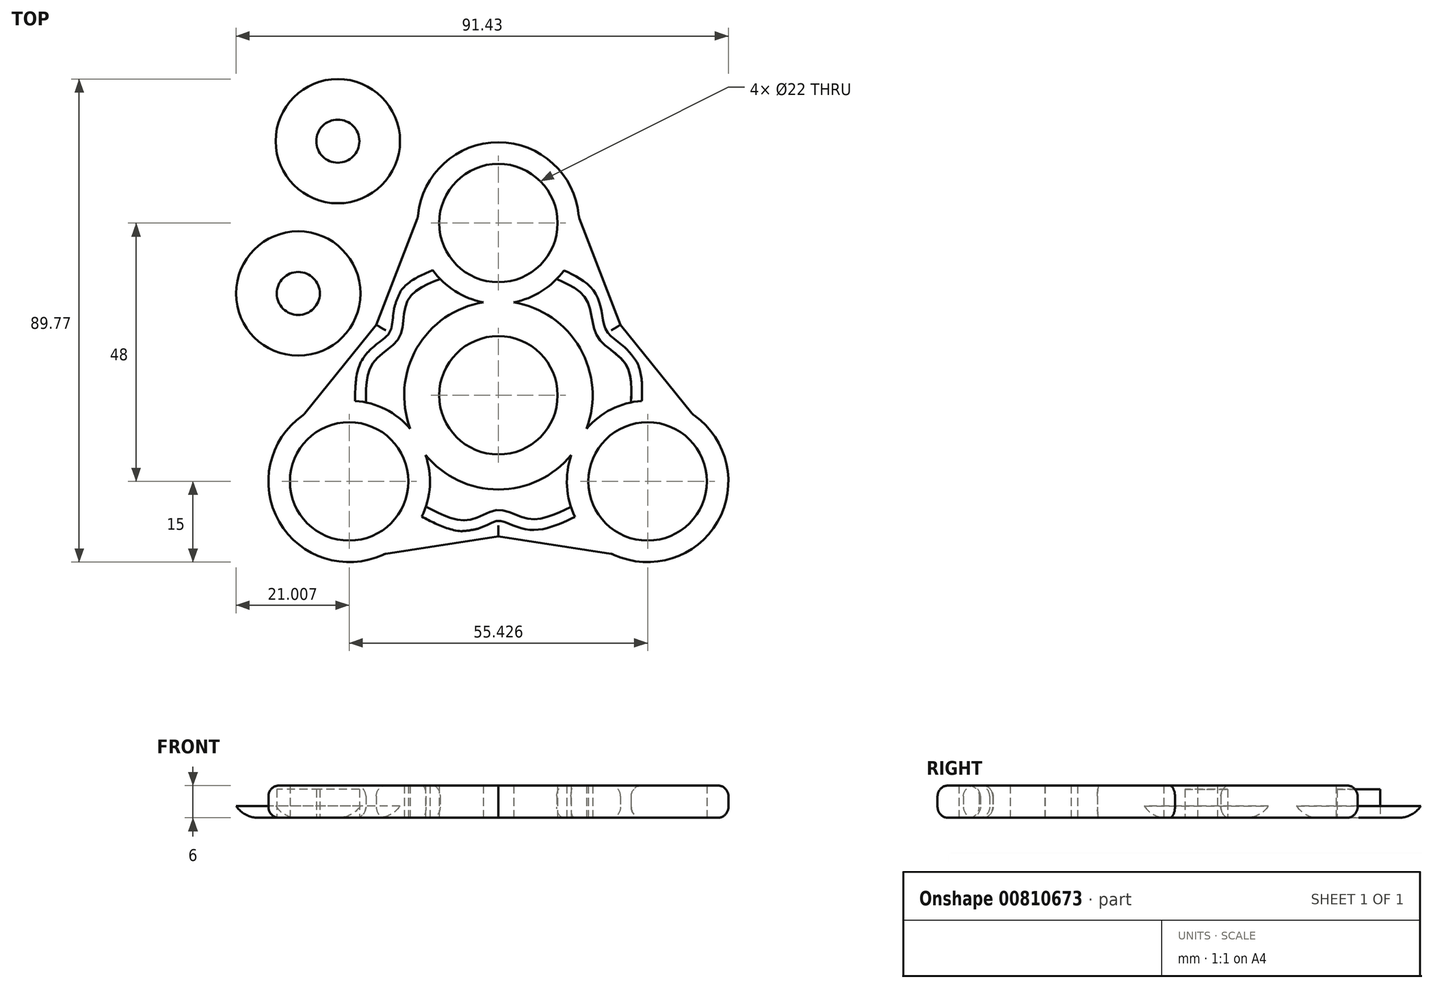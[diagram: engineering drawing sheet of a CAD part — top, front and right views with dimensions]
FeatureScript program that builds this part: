
annotation { "Feature Type Name" : "Feature", "Feature Type Description" : "" }
export const myFeature = defineFeature(function(context is Context, id is Id, definition is map)
    precondition{}
    {
        {
            var Q0;
            Q0=qCreatedBy(makeId("Top.planeOp"),FACE);
            var sketch = newSketch(context, id + "F0", { "sketchPlane" : qUnion([Q0])});
            skCircle(sketch, "E0", {"center": v(0, 0) * mm, "radius": 11 * mm});
            skArc(sketch, "E1", {"start": v(-2.83, 17.27) * mm, "mid": v(-15.16, 8.75) * mm, "end": v(-16.37, -6.18) * mm});
            skCircle(sketch, "E2", {"center": v(0, 32) * mm, "radius": 11 * mm});
            skArc(sketch, "E3", {"start": v(2.83, 17.27) * mm, "mid": v(7.17, 18.82) * mm, "end": v(10.83, 21.62) * mm});
            skLineSegment(sketch, "E4", {"start": v(-14.96, 33.08) * mm, "end": v(-22.68, 13.1) * mm});
            skLineSegment(sketch, "E5", {"start": v(14.96, 33.08) * mm, "end": v(22.68, 13.1) * mm});
            skArc(sketch, "E6.1.0", {"start": v(-16.37, -6.18) * mm, "mid": v(-20.1, -3.08) * mm, "end": v(-24.6, -1.32) * mm});
            skCircle(sketch, "E6.1.1", {"center": v(-27.71, -16) * mm, "radius": 11 * mm});
            skLineSegment(sketch, "E6.1.2", {"start": v(-21.17, -29.5) * mm, "end": v(0, -26.19) * mm});
            skLineSegment(sketch, "E6.1.3", {"start": v(-36.13, -3.59) * mm, "end": v(-22.68, 13.1) * mm});
            skArc(sketch, "E6.1.5", {"start": v(-13.54, -11.09) * mm, "mid": v(0, -17.5) * mm, "end": v(13.54, -11.09) * mm});
            skArc(sketch, "E6.2.0", {"start": v(13.54, -11.09) * mm, "mid": v(12.71, -15.9) * mm, "end": v(13.48, -20.74) * mm});
            skCircle(sketch, "E6.2.1", {"center": v(27.71, -16) * mm, "radius": 11 * mm});
            skLineSegment(sketch, "E6.2.2", {"start": v(36.13, -3.59) * mm, "end": v(22.68, 13.1) * mm});
            skLineSegment(sketch, "E6.2.3", {"start": v(21.17, -29.5) * mm, "end": v(0, -26.19) * mm});
            skArc(sketch, "E6.2.5", {"start": v(16.37, -6.18) * mm, "mid": v(15.16, 8.75) * mm, "end": v(2.83, 17.27) * mm});
            skPoint(sketch, "E7.1.internal.orphan", {"position": v(-16.89, 17.59) * mm});
            skPoint(sketch, "E7.start.orphan", {"position": v(-10.83, 21.62) * mm});
            skPoint(sketch, "E8.0.internal.orphan", {"position": v(10.83, 21.62) * mm});
            skPoint(sketch, "E8.1.internal.orphan", {"position": v(16.46, 17.59) * mm});
            skFitSpline(sketch, "E9", {"points": [v(10.83, 21.62) * mm, v(16.46, 17.59) * mm, v(18.38, 10.94) * mm, v(23.55, 5.93) * mm, v(24.6, -1.32) * mm], "startDerivative": vector(28.02, -12.83) * mm, "endDerivative": vector(-1.42, -31.6) * mm});
            skFitSpline(sketch, "E10", {"points": [v(-10.83, 21.62) * mm, v(-16.89, 17.59) * mm, v(-18.39, 10.82) * mm, v(-23.25, 6.09) * mm, v(-24.6, -1.32) * mm], "startDerivative": vector(-30.09, -12.11) * mm, "endDerivative": vector(0.1, -32.23) * mm});
            skFitSpline(sketch, "E11", {"points": [v(-13.46, -20.68) * mm, v(-5.62, -23.22) * mm, v(0, -21.3) * mm, v(5.7, -22.98) * mm, v(13.48, -20.74) * mm], "startDerivative": vector(30.2, -15.88) * mm, "endDerivative": vector(30.13, 14.3) * mm});
            skArc(sketch, "E12.trimOffspring", {"start": v(-13.46, -20.68) * mm, "mid": v(-12.71, -15.88) * mm, "end": v(-13.54, -11.09) * mm});
            skArc(sketch, "E13.trimOffspring", {"start": v(21.17, -29.5) * mm, "mid": v(40.7, -23.5) * mm, "end": v(36.13, -3.59) * mm});
            skArc(sketch, "E14.trimOffspring", {"start": v(-36.13, -3.59) * mm, "mid": v(-40.7, -23.5) * mm, "end": v(-21.17, -29.5) * mm});
            skArc(sketch, "E15.trimOffspring", {"start": v(-10.83, 21.62) * mm, "mid": v(-7.17, 18.82) * mm, "end": v(-2.83, 17.27) * mm});
            skArc(sketch, "E16.trimOffspring", {"start": v(14.96, 33.08) * mm, "mid": v(0, 47) * mm, "end": v(-14.96, 33.08) * mm});
            skArc(sketch, "E17.trimOffspring", {"start": v(24.6, -1.32) * mm, "mid": v(20.1, -3.08) * mm, "end": v(16.37, -6.18) * mm});
            skSolve(sketch);
        }
        {
            var Q0;
            Q0 = qSketchRegion(id + "F0", true);
            extrude(context, id + "F1", {"entities" : qUnion([Q0]), "depth" : 6 * mm, "offsetDistance" : 25 * mm});
        }
        {
            var Q0;
            Q0=makeQuery(id+"F1.opExtrude","CAP_EDGE",EDGE,{"disambiguationData":[OSD([sQuery(id+"F0.wireOp",EDGE,"E5")])],"isStart":false});
            var Q1;
            Q1=makeQuery(id+"F1.opExtrude","CAP_EDGE",EDGE,{"disambiguationData":[OSD([sQuery(id+"F0.wireOp",EDGE,"E5")])],"isStart":true});
            var Q2;
            Q2=makeQuery(id+"F1.opExtrude","SWEPT_FACE",FACE,{"disambiguationData":[OSD([sQuery(id+"F0.wireOp",EDGE,"E16.trimOffspring")])]});
            var Q3;
            Q3=makeQuery(id+"F1.opExtrude","CAP_EDGE",EDGE,{"disambiguationData":[OSD([sQuery(id+"F0.wireOp",EDGE,"E6.2.2")])],"isStart":false});
            var Q4;
            Q4=makeQuery(id+"F1.opExtrude","CAP_EDGE",EDGE,{"disambiguationData":[OSD([sQuery(id+"F0.wireOp",EDGE,"E6.2.2")])],"isStart":true});
            var Q5;
            Q5=makeQuery(id+"F1.opExtrude","CAP_EDGE",EDGE,{"disambiguationData":[OSD([sQuery(id+"F0.wireOp",EDGE,"E4")])],"isStart":false});
            var Q6;
            Q6=makeQuery(id+"F1.opExtrude","CAP_EDGE",EDGE,{"disambiguationData":[OSD([sQuery(id+"F0.wireOp",EDGE,"E4")])],"isStart":true});
            var Q7;
            Q7=makeQuery(id+"F1.opExtrude","CAP_EDGE",EDGE,{"disambiguationData":[OSD([sQuery(id+"F0.wireOp",EDGE,"E6.1.3")])],"isStart":false});
            var Q8;
            Q8=makeQuery(id+"F1.opExtrude","CAP_EDGE",EDGE,{"disambiguationData":[OSD([sQuery(id+"F0.wireOp",EDGE,"E6.1.3")])],"isStart":true});
            var Q9;
            Q9=makeQuery(id+"F1.opExtrude","SWEPT_FACE",FACE,{"disambiguationData":[OSD([sQuery(id+"F0.wireOp",EDGE,"E14.trimOffspring")])]});
            var Q10;
            Q10=makeQuery(id+"F1.opExtrude","CAP_EDGE",EDGE,{"disambiguationData":[OSD([sQuery(id+"F0.wireOp",EDGE,"E6.2.3")])],"isStart":true});
            var Q11;
            Q11=makeQuery(id+"F1.opExtrude","CAP_EDGE",EDGE,{"disambiguationData":[OSD([sQuery(id+"F0.wireOp",EDGE,"E6.2.3")])],"isStart":false});
            var Q12;
            Q12=makeQuery(id+"F1.opExtrude","CAP_EDGE",EDGE,{"disambiguationData":[OSD([sQuery(id+"F0.wireOp",EDGE,"E6.1.2")])],"isStart":true});
            var Q13;
            Q13=makeQuery(id+"F1.opExtrude","CAP_EDGE",EDGE,{"disambiguationData":[OSD([sQuery(id+"F0.wireOp",EDGE,"E6.1.2")])],"isStart":false});
            var Q14;
            Q14=makeQuery(id+"F1.opExtrude","SWEPT_FACE",FACE,{"disambiguationData":[OSD([sQuery(id+"F0.wireOp",EDGE,"E13.trimOffspring")])]});
            var Q15;
            Q15=makeQuery(id+"F1.opExtrude","CAP_EDGE",EDGE,{"disambiguationData":[OSD([sQuery(id+"F0.wireOp",EDGE,"E9")])],"isStart":true});
            var Q16;
            Q16=makeQuery(id+"F1.opExtrude","CAP_EDGE",EDGE,{"disambiguationData":[OSD([sQuery(id+"F0.wireOp",EDGE,"E9")])],"isStart":false});
            var Q17;
            Q17=makeQuery(id+"F1.opExtrude","CAP_EDGE",EDGE,{"disambiguationData":[OSD([sQuery(id+"F0.wireOp",EDGE,"E11")])],"isStart":true});
            var Q18;
            Q18=makeQuery(id+"F1.opExtrude","CAP_EDGE",EDGE,{"disambiguationData":[OSD([sQuery(id+"F0.wireOp",EDGE,"E11")])],"isStart":false});
            var Q19;
            Q19=makeQuery(id+"F1.opExtrude","CAP_EDGE",EDGE,{"disambiguationData":[OSD([sQuery(id+"F0.wireOp",EDGE,"E10")])],"isStart":true});
            var Q20;
            Q20=makeQuery(id+"F1.opExtrude","CAP_EDGE",EDGE,{"disambiguationData":[OSD([sQuery(id+"F0.wireOp",EDGE,"E10")])],"isStart":false});
            var Q21;
            Q21=makeQuery(id+"F1.opExtrude","SWEPT_FACE",FACE,{"disambiguationData":[OSD([sQuery(id+"F0.wireOp",EDGE,"E1")])]});
            var Q22;
            Q22=makeQuery(id+"F1.opExtrude","SWEPT_FACE",FACE,{"disambiguationData":[OSD([sQuery(id+"F0.wireOp",EDGE,"E6.2.5")])]});
            var Q23;
            Q23=makeQuery(id+"F1.opExtrude","SWEPT_FACE",FACE,{"disambiguationData":[OSD([sQuery(id+"F0.wireOp",EDGE,"E6.1.5")])]});
            fillet(context, id + "F2", {"entities" : qUnion([Q0, Q1, Q2, Q3, Q4, Q5, Q6, Q7, Q8, Q9, Q10, Q11, Q12, Q13, Q14, Q15, Q16, Q17, Q18, Q19, Q20, Q21, Q22, Q23]), "radius" : 2 * mm, "tangentPropagation" : true, "allowEdgeOverflow" : false});
        }
        {
            var Q0;
            Q0=qCreatedBy(makeId("Top.planeOp"),FACE);
            var sketch = newSketch(context, id + "F3", { "sketchPlane" : qUnion([Q0])});
            skCircle(sketch, "E18", {"center": v(-37.17, 18.91) * mm, "radius": 11.55 * mm});
            skCircle(sketch, "E19", {"center": v(-37.17, 18.91) * mm, "radius": 4 * mm});
            skCircle(sketch, "E20", {"center": v(-29.82, 47.22) * mm, "radius": 11.55 * mm});
            skCircle(sketch, "E21", {"center": v(-29.82, 47.22) * mm, "radius": 4 * mm});
            skSolve(sketch);
        }
        {
            var Q0;
            Q0 = qSketchRegion(id + "F3", true);
            var Q1;
            Q1=makeQuery(id+"F3.imprint","IMPRINT",FACE,{"disambiguationData":[TD([[makeQuery(id+"F3.imprint","IMPRINT",EDGE,{"derivedFrom":sQuery(id+"F3.wireOp",EDGE,"E19")}),1.0]])]});
            var Q2;
            Q2=makeQuery(id+"F3.imprint","IMPRINT",FACE,{"disambiguationData":[TD([[makeQuery(id+"F3.imprint","IMPRINT",EDGE,{"derivedFrom":sQuery(id+"F3.wireOp",EDGE,"E21")}),1.0]])]});
            extrude(context, id + "F4", {"entities" : qUnion([Q0, Q1, Q2]), "operationType" : NewBodyOperationType.ADD, "depth" : 2.2 * mm, "offsetDistance" : 25 * mm});
        }
        {
            var Q0;
            Q0=makeQuery(id+"F3.imprint","IMPRINT",FACE,{"disambiguationData":[TD([[makeQuery(id+"F3.imprint","IMPRINT",EDGE,{"derivedFrom":sQuery(id+"F3.wireOp",EDGE,"E19")}),1.0]])]});
            var Q1;
            Q1=makeQuery(id+"F3.imprint","IMPRINT",FACE,{"disambiguationData":[TD([[makeQuery(id+"F3.imprint","IMPRINT",EDGE,{"derivedFrom":sQuery(id+"F3.wireOp",EDGE,"E21")}),1.0]])]});
            extrude(context, id + "F5", {"entities" : qUnion([Q0, Q1]), "depth" : 5.3 * mm, "offsetDistance" : 25 * mm});
        }
        {
            var Q0;
            Q0=makeQuery(id+"F4.opExtrude","CAP_EDGE",EDGE,{"disambiguationData":[OSD([sQuery(id+"F3.wireOp",EDGE,"E20")])],"isStart":true});
            var Q1;
            Q1=makeQuery(id+"F4.opExtrude","CAP_EDGE",EDGE,{"disambiguationData":[OSD([sQuery(id+"F3.wireOp",EDGE,"E18")])],"isStart":true});
            fillet(context, id + "F6", {"entities" : qUnion([Q0, Q1]), "radius" : 5 * mm, "tangentPropagation" : true, "allowEdgeOverflow" : false});
        }
    });
